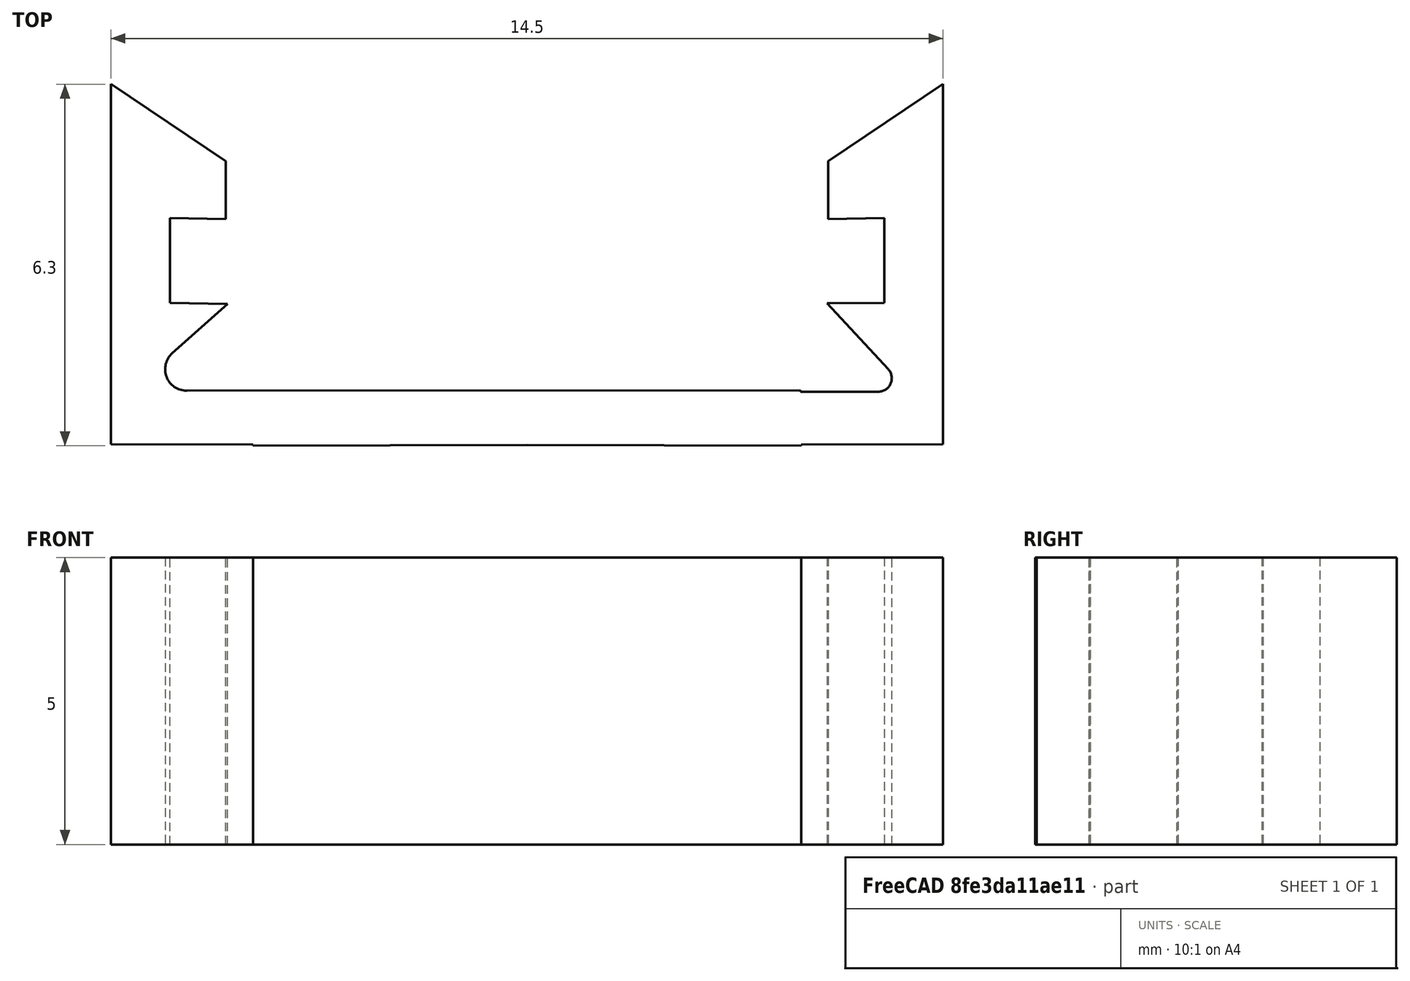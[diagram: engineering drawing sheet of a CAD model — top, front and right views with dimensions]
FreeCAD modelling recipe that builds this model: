
FCSTD DOCUMENT  (FreeCAD 0.18.4R)
Label: 12mmClip
License: All rights reserved
LicenseURL: http://en.wikipedia.org/wiki/All_rights_reserved
objects: Sketcher::SketchObject×2, Part::Extrusion×2, Part::MultiFuse×1, Mesh::Feature×1
note: 5 computed .brp shape members not serialized (recipe doc carries the construction recipe); baked Part::Feature solids carry a one-line shape summary decoded from their .brp

FEATURE [Sketcher::SketchObject] Sketch
  sketch-geometry (11):
    g0: LineSegment StartX=-20.0003 StartY=-0.953855 StartZ=0 EndX=-7.97538 EndY=-0.976673 EndZ=0
    g1: LineSegment StartX=-20.0003 StartY=5.32411 StartZ=0 EndX=-20.0003 EndY=-0.953855 EndZ=0
    g2: LineSegment StartX=-20.0003 StartY=5.32411 StartZ=0 EndX=-17.9981 EndY=3.98015 EndZ=0
    g3: LineSegment StartX=-17.9981 StartY=3.98015 StartZ=0 EndX=-17.9981 EndY=2.9731 EndZ=0
    g4: LineSegment StartX=-18.9735 StartY=2.99151 StartZ=0 EndX=-17.9981 EndY=2.9731 EndZ=0
    g5: LineSegment StartX=-18.9735 StartY=2.99151 StartZ=0 EndX=-18.9735 EndY=1.51236 EndZ=0
    g6: LineSegment StartX=-18.9735 StartY=1.51236 StartZ=0 EndX=-17.966 EndY=1.4934 EndZ=0
    g7: LineSegment StartX=-17.966 StartY=1.4934 StartZ=0 EndX=-18.9306 EndY=0.632583 EndZ=0
    g8: LineSegment StartX=-18.6816 StartY=-0.0198131 StartZ=0 EndX=-7.98357 EndY=-0.0148547 EndZ=0
    g9: LineSegment StartX=-7.98357 StartY=-0.0148547 StartZ=0 EndX=-7.97538 EndY=-0.976673 EndZ=0
    g10: ArcOfCircle CenterX=-18.6818 CenterY=0.353817 CenterZ=0 NormalX=0 NormalY=0 NormalZ=1 AngleXU=0 Radius=0.37363 StartAngle=2.29941 EndAngle=4.71285
  constraints (11):
    c: Coincident(g1,g0)
    c: Coincident(g1,g2)
    c: Coincident(g2,g3)
    c: Coincident(g3,g4)
    c: Coincident(g4,g5)
    c: Coincident(g5,g6)
    c: Coincident(g6,g7)
    c: Coincident(g8,g9)
    c: Coincident(g0,g9)
    c: Tangent(g7,g10) = -1.5708
    c: Tangent(g8,g10) = -1.5708
FEATURE [Part::Extrusion] Extrude
  Base = -> Sketch
  Dir = (0,0,1)
  DirMode = 2
  FaceMakerClass = Part::FaceMakerBullseye
  LengthFwd = 5
  LengthRev = 0
  Solid = true
  Symmetric = false
FEATURE [Sketcher::SketchObject] Sketch001
  sketch-geometry (11):
    g0: LineSegment StartX=-20.0003 StartY=-0.953855 StartZ=0 EndX=-7.97538 EndY=-0.976673 EndZ=0
    g1: LineSegment StartX=-20.0003 StartY=5.32411 StartZ=0 EndX=-20.0003 EndY=-0.953855 EndZ=0
    g2: LineSegment StartX=-20.0003 StartY=5.32411 StartZ=0 EndX=-17.9981 EndY=3.98015 EndZ=0
    g3: LineSegment StartX=-17.9981 StartY=3.98015 StartZ=0 EndX=-17.9981 EndY=2.9731 EndZ=0
    g4: LineSegment StartX=-18.9735 StartY=2.99151 StartZ=0 EndX=-17.9981 EndY=2.9731 EndZ=0
    g5: LineSegment StartX=-18.9735 StartY=2.99151 StartZ=0 EndX=-18.9735 EndY=1.51236 EndZ=0
    g6: LineSegment StartX=-18.9735 StartY=1.51236 StartZ=0 EndX=-17.9772 EndY=1.50391 EndZ=0
    g7: LineSegment StartX=-17.9772 StartY=1.50391 StartZ=0 EndX=-19.0426 EndY=0.355418 EndZ=0
    g8: LineSegment StartX=-18.8705 StartY=-0.038647 StartZ=0 EndX=-7.98363 EndY=-0.0322915 EndZ=0
    g9: LineSegment StartX=-7.98363 StartY=-0.0322915 StartZ=0 EndX=-7.97538 EndY=-0.976673 EndZ=0
    g10: ArcOfCircle CenterX=-18.8706 CenterY=0.195904 CenterZ=0 NormalX=0 NormalY=0 NormalZ=1 AngleXU=0 Radius=0.234551 StartAngle=2.39372 EndAngle=4.71297
  constraints (11):
    c: Coincident(g1,g0)
    c: Coincident(g1,g2)
    c: Coincident(g2,g3)
    c: Coincident(g3,g4)
    c: Coincident(g4,g5)
    c: Coincident(g5,g6)
    c: Coincident(g6,g7)
    c: Coincident(g8,g9)
    c: Coincident(g0,g9)
    c: Tangent(g7,g10) = -1.5708
    c: Tangent(g8,g10) = -1.5708
FEATURE [Part::Extrusion] Extrude001
  Base = -> Sketch001
  Dir = (0,0,1)
  DirMode = 2
  FaceMakerClass = Part::FaceMakerBullseye
  LengthFwd = 5
  LengthRev = 0
  Placement = pos=(-25.5,0,5) rot=(0,1,0;3.14159rad)
  Solid = true
  Symmetric = false
FEATURE [Part::MultiFuse] Fusion
  Shapes = -> [Extrude001,Extrude]
FEATURE [Mesh::Feature] Mesh  label="Fusion (Meshed)"
